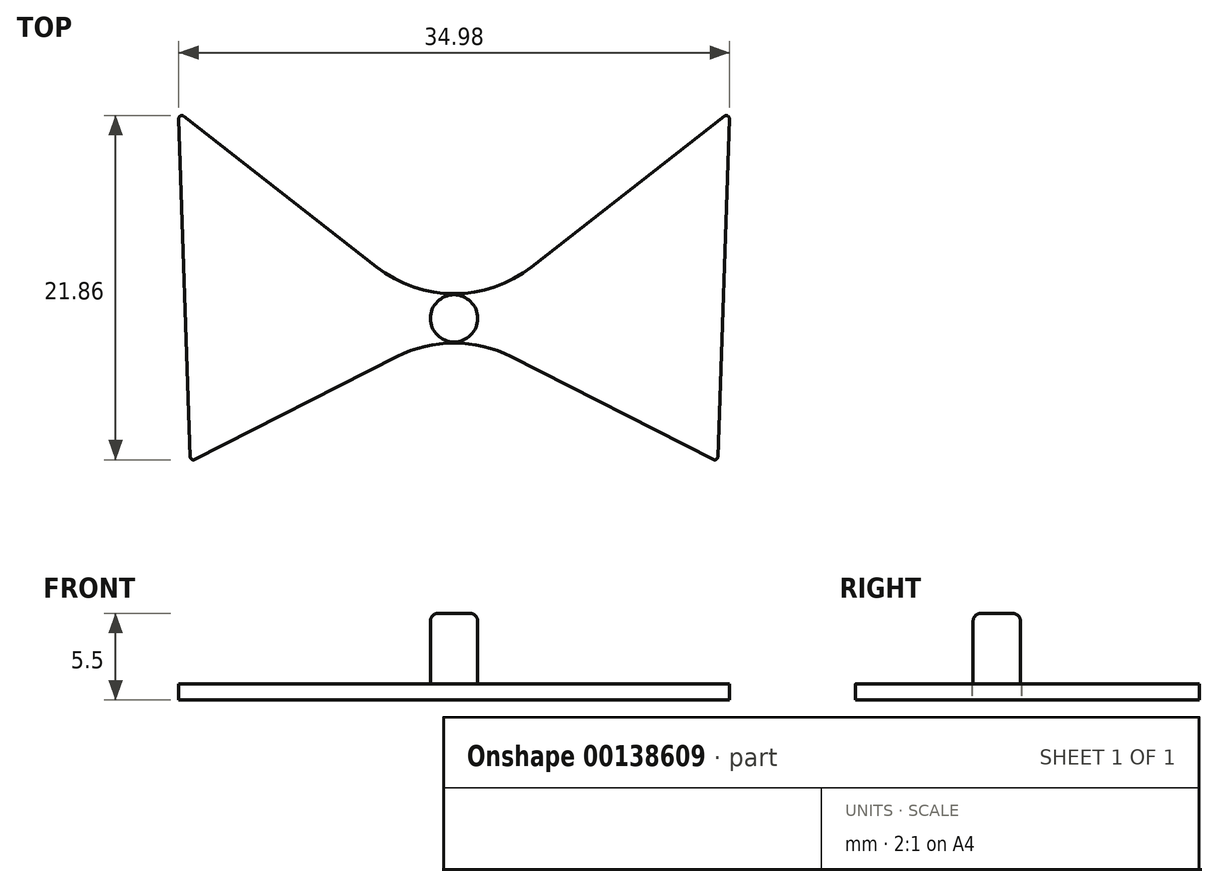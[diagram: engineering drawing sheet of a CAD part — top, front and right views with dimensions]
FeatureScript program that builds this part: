
annotation { "Feature Type Name" : "Feature", "Feature Type Description" : "" }
export const myFeature = defineFeature(function(context is Context, id is Id, definition is map)
    precondition{}
    {
        {
            assignVariable(context, id + "F0", {"name" : "pin_length", "anyValue" : 4.5 * mm});
        }
        {
            assignVariable(context, id + "F1", {"name" : "pin_end_fillet", "anyValue" : 0.5 * mm});
        }
        {
            var Q0;
            Q0=qCreatedBy(makeId("Top.planeOp"),FACE);
            var sketch = newSketch(context, id + "F2", { "sketchPlane" : qUnion([Q0])});
            skLineSegment(sketch, "E0", {"start": v(4.93, 3.86) * mm, "end": v(17.16, 13.43) * mm});
            skLineSegment(sketch, "E1", {"start": v(17.49, 13.27) * mm, "end": v(16.75, -8.2) * mm});
            skLineSegment(sketch, "E2", {"start": v(16.46, -8.37) * mm, "end": v(3.63, -1.84) * mm});
            skLineSegment(sketch, "E3", {"start": v(0, 0) * mm, "end": v(0, 18.66) * mm, "construction": true});
            skLineSegment(sketch, "E4.MirrorCS", {"start": v(-4.93, 3.86) * mm, "end": v(-17.16, 13.43) * mm});
            skLineSegment(sketch, "E5.MirrorCS", {"start": v(-17.49, 13.27) * mm, "end": v(-16.75, -8.2) * mm});
            skLineSegment(sketch, "E6.MirrorCS", {"start": v(-16.46, -8.37) * mm, "end": v(-3.63, -1.84) * mm});
            skPoint(sketch, "E7.visualSharp", {"position": v(0, 0) * mm});
            skArc(sketch, "E7.filletArc", {"start": v(-4.93, 3.86) * mm, "mid": v(0, 2.16) * mm, "end": v(4.93, 3.86) * mm});
            skArc(sketch, "E8.filletArc", {"start": v(3.63, -1.84) * mm, "mid": v(0, -0.97) * mm, "end": v(-3.63, -1.84) * mm});
            skPoint(sketch, "E9.visualSharp", {"position": v(17.5, 13.7) * mm});
            skArc(sketch, "E9.filletArc", {"start": v(17.49, 13.27) * mm, "mid": v(17.38, 13.45) * mm, "end": v(17.16, 13.43) * mm});
            skPoint(sketch, "E10.visualSharp", {"position": v(16.74, -8.51) * mm});
            skArc(sketch, "E10.filletArc", {"start": v(16.46, -8.37) * mm, "mid": v(16.65, -8.37) * mm, "end": v(16.75, -8.2) * mm});
            skPoint(sketch, "E11.visualSharp", {"position": v(-17.5, 13.7) * mm});
            skArc(sketch, "E11.filletArc", {"start": v(-17.16, 13.43) * mm, "mid": v(-17.38, 13.45) * mm, "end": v(-17.49, 13.27) * mm});
            skPoint(sketch, "E12.visualSharp", {"position": v(-16.74, -8.51) * mm});
            skArc(sketch, "E12.filletArc", {"start": v(-16.75, -8.2) * mm, "mid": v(-16.65, -8.37) * mm, "end": v(-16.46, -8.37) * mm});
            skSolve(sketch);
        }
        {
            var Q0;
            Q0=makeQuery(id+"F2.imprint","IMPRINT",FACE,{"disambiguationData":[TD([[makeQuery(id+"F2.imprint","IMPRINT",EDGE,{"derivedFrom":sQuery(id+"F2.wireOp",EDGE,"E0")}),-1.0]])]});
            extrude(context, id + "F3", {"entities" : qUnion([Q0]), "depth" : 1 * mm});
        }
        {
            var Q0;
            Q0=makeQuery(id+"F3.opExtrude","CAP_FACE",FACE,{"disambiguationData":[OSD([sQuery(id+"F2.wireOp",EDGE,"E0"),sQuery(id+"F2.wireOp",EDGE,"E1"),sQuery(id+"F2.wireOp",EDGE,"E2"),sQuery(id+"F2.wireOp",EDGE,"E4.MirrorCS"),sQuery(id+"F2.wireOp",EDGE,"E5.MirrorCS"),sQuery(id+"F2.wireOp",EDGE,"E6.MirrorCS"),sQuery(id+"F2.wireOp",EDGE,"E7.filletArc"),sQuery(id+"F2.wireOp",EDGE,"E8.filletArc"),sQuery(id+"F2.wireOp",EDGE,"E9.filletArc"),sQuery(id+"F2.wireOp",EDGE,"E10.filletArc"),sQuery(id+"F2.wireOp",EDGE,"E11.filletArc"),sQuery(id+"F2.wireOp",EDGE,"E12.filletArc")])],"isStart":false});
            var sketch = newSketch(context, id + "F4", { "sketchPlane" : qUnion([Q0])});
            skArc(sketch, "E13.0", {"start": v(-4.93, 3.86) * mm, "mid": v(0, 2.16) * mm, "end": v(4.93, 3.86) * mm});
            skArc(sketch, "E13.1", {"start": v(3.63, -1.84) * mm, "mid": v(0, -0.97) * mm, "end": v(-3.63, -1.84) * mm});
            skLineSegment(sketch, "E14", {"start": v(0, 2.16) * mm, "end": v(0, -0.97) * mm, "construction": true});
            skCircle(sketch, "E15", {"center": v(0, 0.6) * mm, "radius": 1.5 * mm});
            skSolve(sketch);
        }
        {
            var Q0;
            Q0=makeQuery(id+"F4.imprint","IMPRINT",FACE,{"disambiguationData":[TD([[makeQuery(id+"F4.imprint","IMPRINT",EDGE,{"derivedFrom":sQuery(id+"F4.wireOp",EDGE,"E15")}),1.0]])]});
            var Q1;
            Q1=sQuery(id+"F4.wireOp",EDGE,"E14");
            extrude(context, id + "F5", {"entities" : qUnion([Q0]), "operationType" : NewBodyOperationType.ADD, "surfaceEntities" : qUnion([Q1]), "depth" : getVariable(context, 'pin_length')});
        }
        {
            var Q0;
            Q0=makeQuery(id+"F5.opExtrude","CAP_EDGE",EDGE,{"disambiguationData":[OSD([sQuery(id+"F4.wireOp",EDGE,"E15")])],"isStart":false});
            fillet(context, id + "F6", {"entities" : qUnion([Q0]), "radius" : getVariable(context, 'pin_end_fillet'), "tangentPropagation" : true, "allowEdgeOverflow" : false});
        }
    });
